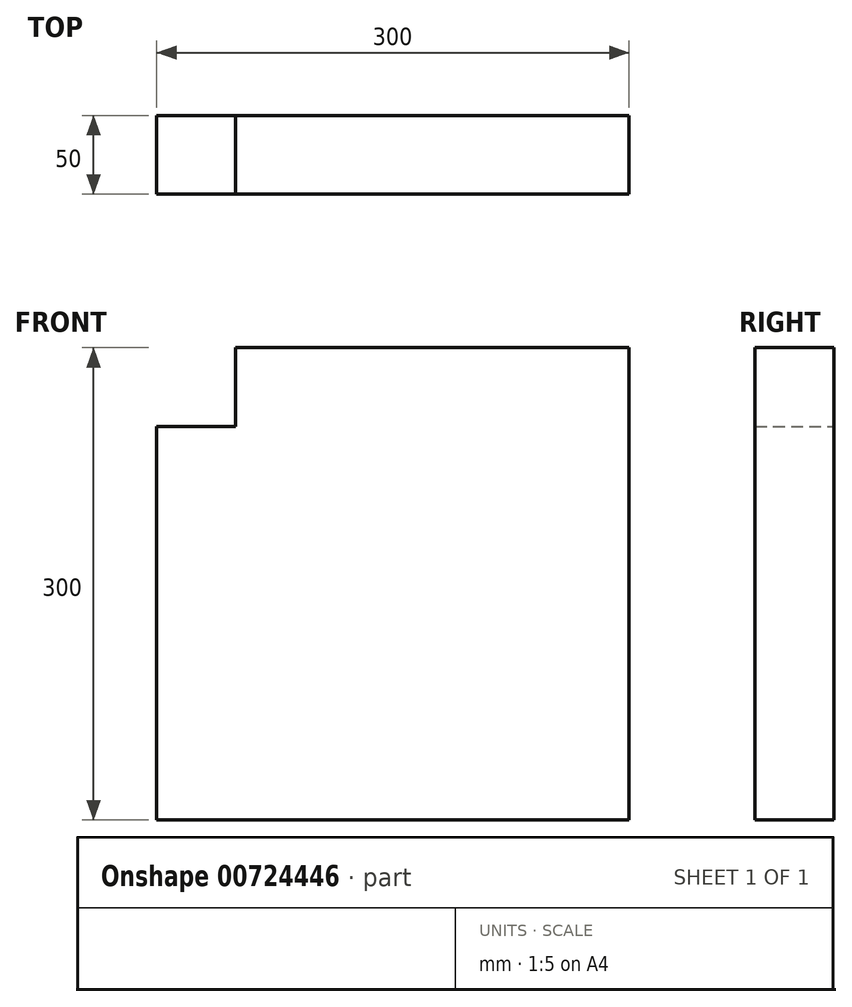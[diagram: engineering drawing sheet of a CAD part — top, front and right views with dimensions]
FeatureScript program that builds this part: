
annotation { "Feature Type Name" : "Feature", "Feature Type Description" : "" }
export const myFeature = defineFeature(function(context is Context, id is Id, definition is map)
    precondition{}
    {
        {
            var Q0;
            Q0=qCreatedBy(makeId("Front.planeOp"),FACE);
            var sketch = newSketch(context, id + "F0", { "sketchPlane" : qUnion([Q0])});
            skLineSegment(sketch, "E0.bottom", {"start": v(-726, 397.2) * mm, "end": v(-476, 397.2) * mm});
            skLineSegment(sketch, "E0.top", {"start": v(-776, 97.2) * mm, "end": v(-476, 97.2) * mm});
            skLineSegment(sketch, "E0.left", {"start": v(-776, 347.2) * mm, "end": v(-776, 97.2) * mm});
            skLineSegment(sketch, "E0.right", {"start": v(-476, 397.2) * mm, "end": v(-476, 97.2) * mm});
            skLineSegment(sketch, "E1.top", {"start": v(-776, 347.2) * mm, "end": v(-726, 347.2) * mm});
            skLineSegment(sketch, "E1.right", {"start": v(-726, 397.2) * mm, "end": v(-726, 347.2) * mm});
            skSolve(sketch);
        }
        {
            var Q0;
            Q0 = qSketchRegion(id + "F0", true);
            extrude(context, id + "F1", {"entities" : qUnion([Q0]), "depth" : 50 * mm, "offsetDistance" : 25 * mm});
        }
    });
